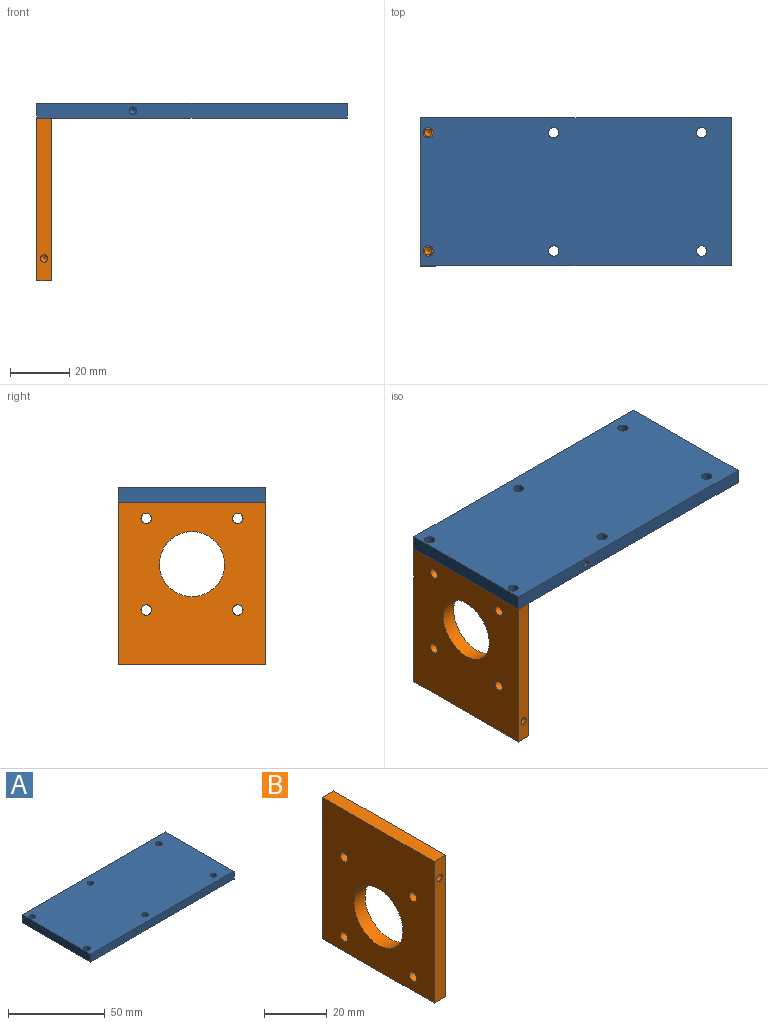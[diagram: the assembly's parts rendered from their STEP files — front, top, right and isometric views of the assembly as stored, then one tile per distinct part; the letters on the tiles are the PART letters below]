
ASSEMBLY  parts=2 mates=1
PART A: 16 faces, bbox 105x50x5 mm
  f0: plane 105x5mm, normal (0,1,0), area 520.1mm2, adj f1,f3,f4,f5,f11
  f1: plane 105x50mm, normal (0,0,1), area 5192.3mm2, adj f0,f2,f3,f4,f6,f7,f8,f9
  f2: plane 105x5mm, normal (0,-1,0), area 520.1mm2, adj f1,f3,f4,f5,f13
  f3: plane 50x5mm, normal (1,0,0), area 250mm2, adj f0,f1,f2,f5
  f4: plane 50x5mm, normal (-1,0,0), area 250mm2, adj f0,f1,f2,f5
  f5: plane 105x50mm, normal (0,0,-1), area 5192.3mm2, adj f0,f2,f3,f4,f6,f7,f8,f9
  f6: cylinder r=1.75mm len=5mm, axis (0,0,-1), area 55mm2, adj f1,f5
  f7: cylinder r=1.75mm len=5mm, axis (0,0,-1), area 55mm2, adj f1,f5
  f8: cylinder r=1.75mm len=5mm, axis (0,0,-1), area 55mm2, adj f1,f5
  f9: cylinder r=1.75mm len=5mm, axis (0,0,-1), area 55mm2, adj f1,f5
  f10: cone r=0mm half-angle=59deg, axis (0,1,0), area 5.7mm2, adj f11
  f11: cylinder r=1.25mm len=3mm, axis (0,1,0), area 23.6mm2, adj f0,f10
  f12: cone r=0mm half-angle=59deg, axis (0,-1,0), area 5.7mm2, adj f13
  f13: cylinder r=1.25mm len=3mm, axis (0,-1,0), area 23.6mm2, adj f2,f12
  f14: cylinder r=1.75mm len=5mm, axis (0,0,-1), area 55mm2, adj f1,f5
  f15: cylinder r=1.75mm len=5mm, axis (0,0,-1), area 55mm2, adj f1,f5
PART B: 19 faces, bbox 5x50x55 mm
  f0: plane 55x5mm, normal (0,-1,0), area 270.1mm2, adj f1,f3,f4,f13,f14
  f1: plane 55x50mm, normal (-1,0,0), area 2330.5mm2, adj f0,f2,f4,f5,f6,f7,f8,f9
  f2: plane 55x5mm, normal (0,1,0), area 270.1mm2, adj f1,f3,f4,f11,f14
  f3: plane 55x50mm, normal (1,0,0), area 2330.5mm2, adj f0,f2,f4,f5,f6,f7,f8,f9
  f4: plane 50x5mm, normal (0,0,1), area 250mm2, adj f0,f1,f2,f3
  f5: cylinder r=11.01mm len=22.03mm, axis (-1,0,0), area 346mm2, adj f1,f3
  f6: cylinder r=1.75mm len=5mm, axis (-1,0,0), area 55mm2, adj f1,f3
  f7: cylinder r=1.75mm len=5mm, axis (-1,0,0), area 55mm2, adj f1,f3
  f8: cylinder r=1.75mm len=5mm, axis (-1,0,0), area 55mm2, adj f1,f3
  f9: cylinder r=1.75mm len=5mm, axis (-1,0,0), area 55mm2, adj f1,f3
  f10: cone r=0mm half-angle=59deg, axis (0,1,0), area 5.7mm2, adj f11
  f11: cylinder r=1.25mm len=3mm, axis (0,1,0), area 23.6mm2, adj f2,f10
  f12: cone r=0mm half-angle=59deg, axis (0,-1,0), area 5.7mm2, adj f13
  f13: cylinder r=1.25mm len=3mm, axis (0,-1,0), area 23.6mm2, adj f0,f12
  f14: plane 50x5mm, normal (0,0,-1), area 240.2mm2, adj f0,f1,f2,f3,f16,f18
  f15: cone r=0mm half-angle=59deg, axis (0,0,-1), area 5.7mm2, adj f16
  f16: cylinder r=1.25mm len=10mm, axis (0,0,-1), area 78.5mm2, adj f14,f15
  f17: cone r=0mm half-angle=59deg, axis (0,0,-1), area 5.7mm2, adj f18
  f18: cylinder r=1.25mm len=10mm, axis (0,0,-1), area 78.5mm2, adj f14,f17
PLACE A t=(-7.24,2.85,8.04)mm
PLACE B rot(axis=(0,1,0),180deg) t=(-107.24,2.85,13.04)mm
MATE fastened B.f17 <-> A.f15  axis (0,0,1) through (-57.24,-17.15,8.04)mm
